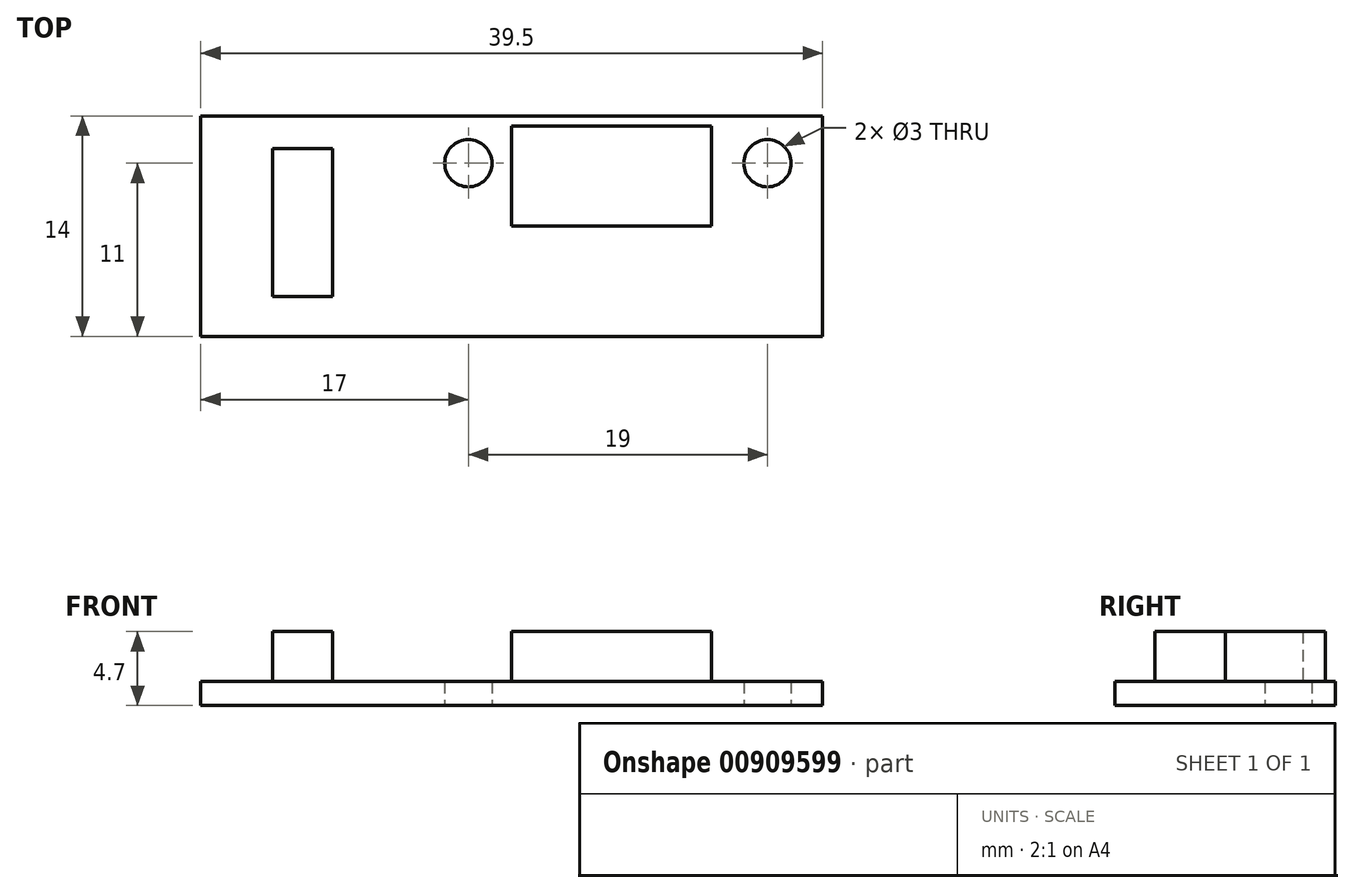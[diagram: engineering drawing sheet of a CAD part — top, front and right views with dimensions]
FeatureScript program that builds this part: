
annotation { "Feature Type Name" : "Feature", "Feature Type Description" : "" }
export const myFeature = defineFeature(function(context is Context, id is Id, definition is map)
    precondition{}
    {
        {
            var Q0;
            Q0=qCreatedBy(makeId("Top.planeOp"),FACE);
            var sketch = newSketch(context, id + "F0", { "sketchPlane" : qUnion([Q0])});
            skLineSegment(sketch, "E0.bottom", {"start": v(19.75, 7) * mm, "end": v(-19.75, 7) * mm});
            skLineSegment(sketch, "E0.top", {"start": v(19.75, -7) * mm, "end": v(-19.75, -7) * mm});
            skLineSegment(sketch, "E0.left", {"start": v(19.75, 7) * mm, "end": v(19.75, -7) * mm});
            skLineSegment(sketch, "E0.right", {"start": v(-19.75, 7) * mm, "end": v(-19.75, -7) * mm});
            skPoint(sketch, "E0.middle", {"position": v(0, 0) * mm});
            skCircle(sketch, "E1", {"center": v(16.25, 4) * mm, "radius": 1.5 * mm});
            skCircle(sketch, "E2", {"center": v(-2.75, 4) * mm, "radius": 1.5 * mm});
            skSolve(sketch);
        }
        {
            var Q0;
            Q0=makeQuery(id+"F0.imprint","IMPRINT",FACE,{"disambiguationData":[TD([[makeQuery(id+"F0.imprint","IMPRINT",EDGE,{"derivedFrom":sQuery(id+"F0.wireOp",EDGE,"E0.bottom")}),1.0]])]});
            extrude(context, id + "F1", {"entities" : qUnion([Q0]), "depth" : 1.52 * mm, "offsetDistance" : 25.4 * mm});
        }
        {
            var Q0;
            Q0=makeQuery(id+"F1.opExtrude","CAP_FACE",FACE,{"disambiguationData":[OSD([sQuery(id+"F0.wireOp",EDGE,"E0.bottom"),sQuery(id+"F0.wireOp",EDGE,"E0.top"),sQuery(id+"F0.wireOp",EDGE,"E0.left"),sQuery(id+"F0.wireOp",EDGE,"E0.right"),sQuery(id+"F0.wireOp",EDGE,"E1"),sQuery(id+"F0.wireOp",EDGE,"E2")])],"isStart":false});
            var sketch = newSketch(context, id + "F2", { "sketchPlane" : qUnion([Q0])});
            skLineSegment(sketch, "E3.bottom", {"start": v(-15.18, 4.94) * mm, "end": v(-11.37, 4.94) * mm});
            skLineSegment(sketch, "E3.top", {"start": v(-15.18, -4.46) * mm, "end": v(-11.37, -4.46) * mm});
            skLineSegment(sketch, "E3.left", {"start": v(-15.18, 4.94) * mm, "end": v(-15.18, -4.46) * mm});
            skLineSegment(sketch, "E3.right", {"start": v(-11.37, 4.94) * mm, "end": v(-11.37, -4.46) * mm});
            skLineSegment(sketch, "E4.bottom", {"start": v(0, 6.35) * mm, "end": v(12.7, 6.35) * mm});
            skLineSegment(sketch, "E4.top", {"start": v(0, 0) * mm, "end": v(12.7, 0) * mm});
            skLineSegment(sketch, "E4.left", {"start": v(0, 6.35) * mm, "end": v(0, 0) * mm});
            skLineSegment(sketch, "E4.right", {"start": v(12.7, 6.35) * mm, "end": v(12.7, 0) * mm});
            skSolve(sketch);
        }
        {
            var Q0;
            Q0=makeQuery(id+"F2.imprint","IMPRINT",FACE,{"disambiguationData":[TD([[makeQuery(id+"F2.imprint","IMPRINT",EDGE,{"derivedFrom":sQuery(id+"F2.wireOp",EDGE,"E3.bottom")}),-1.0]])]});
            var Q1;
            Q1=makeQuery(id+"F2.imprint","IMPRINT",FACE,{"disambiguationData":[TD([[makeQuery(id+"F2.imprint","IMPRINT",EDGE,{"derivedFrom":sQuery(id+"F2.wireOp",EDGE,"E4.bottom")}),-1.0]])]});
            extrude(context, id + "F3", {"entities" : qUnion([Q0, Q1]), "operationType" : NewBodyOperationType.ADD, "depth" : 3.17 * mm, "offsetDistance" : 25.4 * mm});
        }
    });
